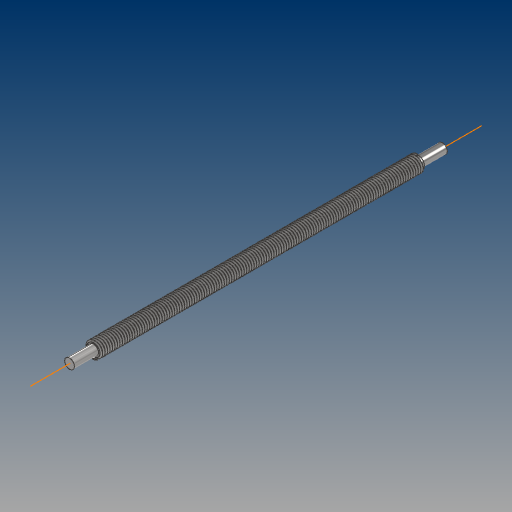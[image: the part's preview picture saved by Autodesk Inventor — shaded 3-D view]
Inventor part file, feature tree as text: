
AUTODESK INVENTOR PART (.ipt)
format: ipt  version: 2021 (Build 250183000, 183)  size: 690,176 bytes
history: native  units: mm
features: sketch x2, revolve x1, helix x1, projected_geometry x1
ambient origin geometry x8: Origin, YZ Plane, XZ Plane, XY Plane, X Axis, Y Axis, Z Axis, Center Point
bodies: Solid1 (feature_tree)
feature tree (5):
  revolve  "Revolution1"  [1 undecoded]
  helix  "Coil1"  [1 undecoded]
  sketch  "Sketch1"  dims[d0=4.0mm d1=19.4mm d2=300.0mm]
  sketch  "Sketch2"  dims[d3=5.0mm d4=90.0deg d5=261.2mm d6=60.0deg d7=1.5mm d8=2.0mm d9=261.2mm d10=10.0mm d11=0.0mm d12=90.0deg d13=90.0deg d14=0.0mm d15=0.0mm]
  projected_geometry  "Projected Loop1"
note: 2 required parameter values undecoded (feature->parameter linkage not recoverable at this tier; creation-order binding heuristic only, values carry confidence <= 0.55)